# Revit family: 5903
name_source: partatom
category: Arredi
revit_build: Autodesk Revit 2016 (Build: 20151007_0715(x64)
units: mm (PartAtom-declared; Revit-internal decimal feet)

## family parameters
Basato su piano di lavoro = No
Condiviso = No
Numero OmniClass = 23.40.20.00
Punto di calcolo locali = No
Sempre verticale = Sì
Taglio con vuoti quando caricato = No
Titolo OmniClass = General Furniture and Specialties

## types (1)
- 5903
    Arper - Legs material = Arper - Generic wood 2
    Descrizione = Stool with reconstituted veneer four-leg base and shell, with natural
birchwood effect or stained in four different colours. Shell and base
can be ordered with the same finish or different finishes can be
combined together. A non-washable, removable cover (Item 3921) is
also available in leather, faux leather, fabric or customer's material.
Optional glides with felt for wooden floors are available upon
request. Seat height 77 cm.
    Modello = Aava
    Produttore = ARPER s.p.a.
    URL = http://www.arper.com
